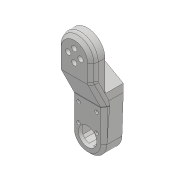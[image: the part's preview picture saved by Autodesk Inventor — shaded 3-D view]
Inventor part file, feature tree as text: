
AUTODESK INVENTOR PART (.ipt)
format: ipt  version: 2018 (Build 220112000, 112)  size: 936,448 bytes
history: native  units: mm
features: projected_geometry x42, sketch x41, extrude x34, fillet x13, chamfer x11, hole x8, other x4, mirror x1, reference x1
ambient origin geometry x8: Origin, YZ Plane, XZ Plane, XY Plane, X Axis, Y Axis, Z Axis, Center Point
bodies: Solid1 (feature_tree)
feature tree (155):
  extrude  "Extrusion1"  Depth=45.0mm
  extrude  "Extrusion2"  Depth=2.25mm
  hole  "Hole1"  [1 undecoded]
  hole  "Hole2"  [1 undecoded]
  fillet  "Fillet1"  Radius=14.0mm
  extrude  "Extrusion3"  Depth=18.5mm
  extrude  "Extrusion4"  Depth=10.0mm
  extrude  "Extrusion5"  Depth=2.195mm
  extrude  "Extrusion6"  Depth=20.5mm
  hole  "Hole3"  [1 undecoded]
  extrude  "Extrusion7"  Depth=0.5mm
  extrude  "Extrusion8"  Depth=5.0mm TaperAngle=0.0deg
  extrude  "Extrusion9"  Depth=10.0mm
  extrude  "Extrusion10"  Depth=10.0mm
  extrude  "Extrusion11"  Depth=14.5mm
  extrude  "Extrusion12"  Depth=14.5mm
  extrude  "Extrusion13"  Depth=5.0mm
  extrude  "Extrusion14"  Depth=2.25mm
  extrude  "Extrusion15"  Depth=5.0mm
  extrude  "Extrusion16"  Depth=9.0mm
  extrude  "Extrusion17"  Depth=4.0mm
  chamfer  "Chamfer1"  Distance=1.0mm
  fillet  "Fillet7"  Radius=20.7mm
  fillet  "Fillet8"  Radius=32.0mm
  mirror  "Mirror1"
  extrude  "Extrusion19"  Depth=1.0mm TaperAngle=0.0deg
  extrude  "Extrusion20"  Depth=8.0mm
  extrude  "Extrusion21"  Depth=0.2mm TaperAngle=0.0deg
  extrude  "Extrusion22"  Depth=0.5mm TaperAngle=0.0deg
  extrude  "Extrusion23"  Depth=9.0mm TaperAngle=0.0deg
  extrude  "Extrusion24"  Depth=0.2mm TaperAngle=0.0deg
  chamfer  "Chamfer2"  Distance=0.2mm
  chamfer  "Chamfer8"  Distance=2.5mm Angle=45.0deg
  extrude  "Extrusion25"  Depth=0.5mm
  extrude  "Extrusion26"  Depth=2.0mm TaperAngle=0.0deg
  chamfer  "Chamfer3"  Distance=2.0mm
  chamfer  "Chamfer4"  Distance=2.0mm
  chamfer  "Chamfer5"  Distance=15.0mm
  chamfer  "Chamfer6"  Distance=56.1mm
  fillet  "Fillet9"  Radius=41.6mm
  fillet  "Fillet10"  Radius=41.0mm
  hole  "Hole6"  [1 undecoded]
  fillet  "Fillet12"  Radius=7.0mm
  hole  "Hole7"  [1 undecoded]
  extrude  "Extrusion27"  Depth=3.0mm TaperAngle=45.0deg
  extrude  "Extrusion28"  Depth=5.0mm TaperAngle=45.0deg
  hole  "Hole8"  [1 undecoded]
  extrude  "Extrusion29"  Depth=10.0mm
  chamfer  "Chamfer7"  Distance=20.5mm
  fillet  "Fillet13"  Radius=1.6mm
  extrude  "Extrusion30"  Depth=10.0mm
  extrude  "Extrusion31"  Depth=10.0mm TaperAngle=0.0deg
  fillet  "Fillet14"  Radius=14.0mm
  extrude  "Extrusion32"  Depth=10.0mm
  fillet  "Fillet15"  Radius=3.1mm
  fillet  "Fillet18"  Radius=1.5mm
  extrude  "Extrusion35"  Depth=10.0mm
  extrude  "Extrusion36"  Depth=10.0mm
  chamfer  "Chamfer9"  Distance=10.0mm
  chamfer  "Chamfer10"  Distance=7.5mm
  chamfer  "Chamfer11"  Distance=6.0mm
  fillet  "Fillet19"  Radius=6.0mm
  hole  "Hole9"  [1 undecoded]
  fillet  "Fillet20"  Radius=6.0mm
  hole  "Hole10"  [1 undecoded]
  fillet  "Fillet21"  Radius=1.5mm
  extrude  "Extrusion37"  Depth=10.0mm
  sketch  "Sketch1"  dims[d0=24.5mm d1=45.0mm]
  sketch  "Sketch2"  dims[d2=1.95mm d3=0.0mm d4=2.25mm]
  projected_geometry  "Projected Loop1"
  sketch  "Sketch3"  dims[d5=20.0mm d6=2.25mm]
  projected_geometry  "Projected Loop2"
  sketch  "Sketch4"  dims[d7=5.25mm d8=5.25mm d9=14.0mm]
  projected_geometry  "Projected Loop3"
  sketch  "Sketch5"  dims[d10=5.25mm d11=18.5mm]
  projected_geometry  "Projected Loop4"
  sketch  "Sketch6"  dims[d12=10.0mm d13=0.0mm d14=20.5mm]
  projected_geometry  "Projected Loop5"
  sketch  "Sketch7"  dims[d15=2.0mm d16=2.195mm]
  projected_geometry  "Projected Loop6"
  sketch  "Sketch8"  dims[d17=2.0mm]
  projected_geometry  "Projected Loop7"
  sketch  "Sketch9"  dims[d18=2.4mm d19=6.0mm d20=4.4mm d21=2.0mm d22=90.0deg d23=8.0mm d24=20.594885mm d25=20.5mm]
  projected_geometry  "Projected Loop8"
  projected_geometry  "Projected Loop9"
  sketch  "Sketch10"  dims[d26=26.65mm d27=2.0mm]
  projected_geometry  "Projected Loop10"
  projected_geometry  "Projected Loop11"
  sketch  "Sketch11"  dims[d28=2.0mm]
  projected_geometry  "Projected Loop12"
  sketch  "Sketch12"  dims[d29=2.4mm d30=6.0mm d31=4.4mm d32=2.0mm d33=90.0deg d34=8.0mm d35=20.594885mm d36=0.5mm]
  sketch  "Sketch13"  dims[d37=18.0mm d38=5.0mm d39=0.0mm]
  sketch  "Sketch14"  dims[d41=10.0mm d42=0.0mm d43=24.5mm]
  projected_geometry  "Projected Loop13"
  sketch  "Sketch15"  dims[d44=1.15mm d45=0.0mm d46=10.0mm]
  sketch  "Sketch16"  dims[d47=21.0mm d48=14.5mm]
  projected_geometry  "Projected Loop14"
  sketch  "Sketch17"  dims[d49=20.0mm d50=14.5mm]
  projected_geometry  "Projected Loop15"
  sketch  "Sketch18"  dims[d51=24.5mm d52=5.0mm]
  projected_geometry  "Projected Loop16"
  sketch  "Sketch19"  dims[d53=5.0mm d54=2.25mm]
  projected_geometry  "Projected Loop17"
  sketch  "Sketch20"  dims[d55=2.25mm d56=5.0mm]
  projected_geometry  "Projected Loop18"
  sketch  "Sketch25"  dims[d57=5.0mm d58=9.0mm]
  projected_geometry  "Projected Loop22"
  sketch  "Sketch26"  dims[d59=14.75mm d60=4.0mm d61=1.0mm d62=0.0mm d63=20.7mm]
  projected_geometry  "Projected Loop23"
  sketch  "Sketch27"  dims[d64=2.4mm d65=6.0mm d66=4.4mm d67=2.0mm d68=90.0deg d69=8.0mm d70=20.594885mm d72=32.0mm]
  projected_geometry  "Projected Loop24"
  sketch  "Sketch28"  dims[d73=5.0mm d74=0.0mm d75=1.0mm d76=0.0mm]
  projected_geometry  "Projected Loop25"
  sketch  "Sketch29"  dims[d77=12.25mm d78=0.0mm d80=8.0mm]
  projected_geometry  "Projected Loop26"
  sketch  "Sketch30"  dims[d81=4.5mm d82=0.0mm d84=0.2mm d85=0.0mm]
  projected_geometry  "Projected Loop27"
  sketch  "Sketch31"  dims[d86=21.0mm d87=0.5mm d88=0.0mm]
  sketch  "Sketch33"  dims[d91=8.0mm d92=0.0mm d93=9.0mm d94=0.0mm]
  projected_geometry  "Projected Loop28"
  projected_geometry  "Projected Loop29"
  projected_geometry  "Projected Loop30"
  sketch  "Sketch34"  dims[d95=5.0mm d96=0.0mm d98=0.2mm d99=0.0mm d100=0.2mm d101=0.0mm d102=2.5mm d103=2.0mm d104=45.0deg]
  projected_geometry  "Projected Loop31"
  projected_geometry  "Projected Loop32"
  sketch  "Sketch35"  dims[d105=1.5mm d114=0.5mm]
  projected_geometry  "Projected Loop33"
  sketch  "Sketch36"  dims[d128=2.0mm d129=0.0mm d130=2.0mm d131=0.0mm]
  projected_geometry  "Projected Loop34"
  sketch  "Sketch37"  dims[d132=40.0mm d133=2.0mm d134=0.0mm d135=2.0mm d136=0.0mm]
  projected_geometry  "Projected Loop35"
  sketch  "Sketch38"  dims[d137=40.0mm]
  projected_geometry  "Projected Loop36"
  sketch  "Sketch39"  dims[d138=70.0mm d139=15.0mm d140=0.0mm d141=56.1mm d142=0.0mm]
  projected_geometry  "Projected Loop37"
  sketch  "Sketch40"  dims[d143=4.0mm d144=8.0mm d145=45.0deg d146=41.6mm d147=41.0mm]
  projected_geometry  "Projected Loop38"
  sketch  "Sketch41"  dims[d148=7.0mm d149=7.0mm d150=7.0mm]
  projected_geometry  "Projected Loop39"
  reference  "Reference1"
  sketch  "Sketch44"  dims[d151=100.0mm d152=0.0mm d153=15.282752mm]
  projected_geometry  "Projected Loop42"
  sketch  "Sketch45"  dims[d156=100.0mm d157=0.0mm d158=3.0mm d159=2.0mm d160=45.0deg]
  projected_geometry  "Projected Loop43"
  sketch  "Sketch46"  dims[d161=5.0mm d162=2.0mm d163=45.0deg d164=5.0mm d165=2.0mm d166=45.0deg]
  projected_geometry  "Projected Loop44"
  sketch  "Sketch47"  dims[d167=5.0mm d168=2.0mm d169=45.0deg d170=5.0mm]
  projected_geometry  "Projected Loop45"
  sketch  "Sketch48"  dims[d171=2.0mm d173=5.7mm d174=6.0mm d175=4.0mm d176=2.0mm d177=90.0deg d178=25.0mm d179=0.0mm d180=1.0mm d181=2.459mm d182=25.0mm d183=4.0mm d184=2.0mm d185=90.0deg d186=25.0mm d187=20.594885mm d188=20.5mm d189=1.6mm d190=0.0mm d191=20.5mm d192=3.1mm d193=0.0mm d194=14.0mm d195=3.2mm d196=25.0mm d197=6.3mm d198=2.0mm d199=90.0deg d200=25.0mm d201=20.594885mm d202=16.0mm d203=3.1mm d204=0.0mm d205=1.5mm d206=2.0mm d207=45.0deg d208=1.7mm d209=37.0mm d210=10.0mm d211=0.0mm d212=7.5mm d213=6.0mm d214=6.0mm d215=6.0mm d216=6.0mm d217=5.0mm d218=0.0mm d219=1.5mm d220=6.0mm d221=6.0mm d222=6.0mm d223=6.0mm d224=6.0mm d225=0.0mm d226=1.5mm d231=4.0mm d232=8.0mm d233=45.0deg d234=10.0mm d237=7.0mm d238=2.5mm d239=0.0mm d240=7.0mm d241=2.5mm d242=0.0mm d243=14.0mm d244=25.0mm d245=45.0deg d246=14.0mm d247=25.0mm d248=45.0deg d249=14.0mm d250=25.0mm d251=45.0deg d252=10.0mm d253=4.0mm d254=6.0mm d255=4.0mm d256=2.0mm d257=90.0deg d258=2.0mm d259=20.594885mm d260=1.0mm d261=4.0mm d262=6.0mm d263=4.0mm d264=2.0mm d265=90.0deg d266=2.0mm d267=20.594885mm d268=1.0mm d269=35.55mm d270=0.0mm]
  projected_geometry  "Project Cut Edges1"
  projected_geometry  "Project Cut Edges2"
  parser-record x1  (decoder bookkeeping rows leaked as tree rows — omitted from the tree; the rows remain in map.json)
  other  "servocheck.iam"
  other  "bottomarm:1"
  other  "arm1:1"
note: 8 required parameter values undecoded (feature->parameter linkage not recoverable at this tier; creation-order binding heuristic only, values carry confidence <= 0.55)
note: 1 file-system path scrubbed to <path> (originals preserved in map.json)
